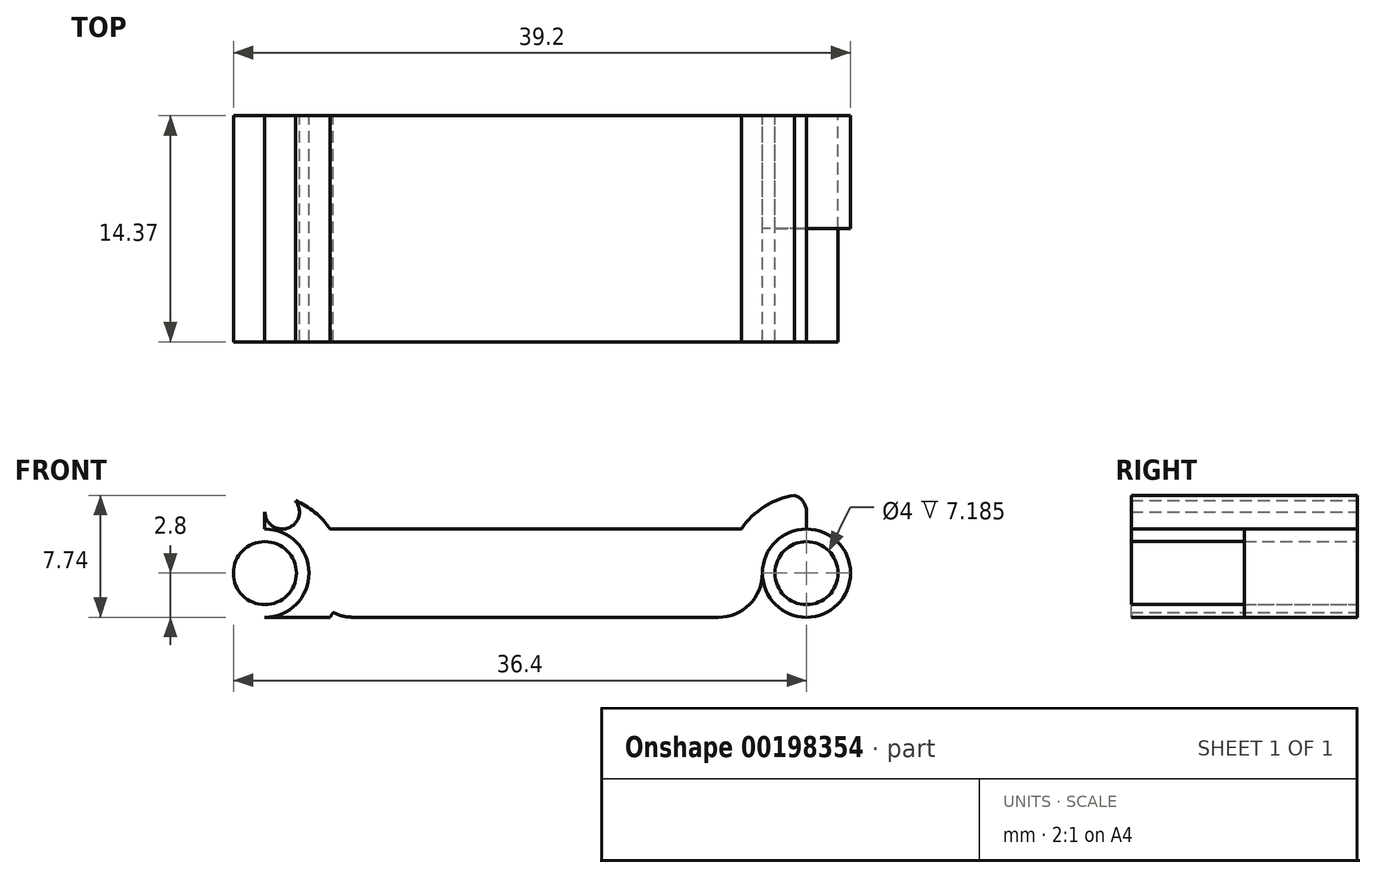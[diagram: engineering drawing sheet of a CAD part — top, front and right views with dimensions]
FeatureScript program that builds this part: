
annotation { "Feature Type Name" : "Feature", "Feature Type Description" : "" }
export const myFeature = defineFeature(function(context is Context, id is Id, definition is map)
    precondition{}
    {
        {
            var Q0;
            Q0=qCreatedBy(makeId("Front.planeOp"),FACE);
            var sketch = newSketch(context, id + "F0", { "sketchPlane" : qUnion([Q0])});
            skLineSegment(sketch, "E0.bottom", {"start": v(2.8, 0) * mm, "end": v(37.2, 0) * mm});
            skLineSegment(sketch, "E0.top", {"start": v(2.8, 5.6) * mm, "end": v(36.1, 5.6) * mm});
            skLineSegment(sketch, "E1.bottom", {"start": v(36.1, 5.6) * mm, "end": v(34.4, 5.6) * mm, "construction": true});
            skLineSegment(sketch, "E1.top", {"start": v(37.2, 0) * mm, "end": v(34.4, 0) * mm, "construction": true});
            skLineSegment(sketch, "E1.right", {"start": v(34.4, 5.6) * mm, "end": v(34.4, 0) * mm, "construction": true});
            skLineSegment(sketch, "E2", {"start": v(34.4, 5.6) * mm, "end": v(40, 0) * mm, "construction": true});
            skCircle(sketch, "E3", {"center": v(37.2, 2.8) * mm, "radius": 2 * mm});
            skCircle(sketch, "E4", {"center": v(37.2, 2.8) * mm, "radius": 2.8 * mm});
            skArc(sketch, "E5", {"start": v(36.45, 7.74) * mm, "mid": v(34.53, 7.03) * mm, "end": v(33.06, 5.6) * mm});
            skArc(sketch, "E6", {"start": v(31.6, 2.8) * mm, "mid": v(36.82, 1.4) * mm, "end": v(33, 5.22) * mm, "construction": true});
            skArc(sketch, "E7", {"start": v(31.6, 0) * mm, "mid": v(33.58, 0.82) * mm, "end": v(34.4, 2.8) * mm});
            skLineSegment(sketch, "E8", {"start": v(37.2, 2.8) * mm, "end": v(37.2, 6.7) * mm, "construction": true});
            skLineSegment(sketch, "E9", {"start": v(37.2, 6.7) * mm, "end": v(37.2, 5.6) * mm});
            skCircle(sketch, "E10", {"center": v(37.2, 6.7) * mm, "radius": 1.1 * mm, "construction": true});
            skArc(sketch, "E11", {"start": v(35.26, 7.4) * mm, "mid": v(36.4, 5.64) * mm, "end": v(36.45, 7.74) * mm});
            skLineSegment(sketch, "E12", {"start": v(20, 5.6) * mm, "end": v(20, 0) * mm, "construction": true});
            skPoint(sketch, "E13.orphan", {"position": v(40, 5.6) * mm});
            skArc(sketch, "E14.trimOffspring", {"start": v(32.74, 0.55) * mm, "mid": v(32.89, 0.27) * mm, "end": v(33.06, 0) * mm});
            skPoint(sketch, "E15.orphan", {"position": v(37.2, 7.8) * mm});
            skLineSegment(sketch, "E16.MirrorCS", {"start": v(2.8, 6.7) * mm, "end": v(2.8, 5.6) * mm});
            skArc(sketch, "E17.MirrorCS", {"start": v(7.26, 0.55) * mm, "mid": v(7.11, 0.27) * mm, "end": v(6.94, 0) * mm});
            skLineSegment(sketch, "E18.MirrorCS", {"start": v(2.8, 2.8) * mm, "end": v(2.8, 6.7) * mm, "construction": true});
            skLineSegment(sketch, "E19.MirrorCS", {"start": v(3.9, 5.6) * mm, "end": v(5.6, 5.6) * mm, "construction": true});
            skLineSegment(sketch, "E20.MirrorCS", {"start": v(2.8, 0) * mm, "end": v(5.6, 0) * mm, "construction": true});
            skArc(sketch, "E21.MirrorCS", {"start": v(4.74, 7.4) * mm, "mid": v(3.6, 5.64) * mm, "end": v(3.55, 7.74) * mm});
            skLineSegment(sketch, "E22.MirrorCS", {"start": v(5.6, 5.6) * mm, "end": v(0, 0) * mm, "construction": true});
            skLineSegment(sketch, "E23.MirrorCS", {"start": v(5.6, 5.6) * mm, "end": v(5.6, 0) * mm, "construction": true});
            skCircle(sketch, "E24.MirrorC", {"center": v(2.8, 6.7) * mm, "radius": 1.1 * mm, "construction": true});
            skArc(sketch, "E25.MirrorCS", {"start": v(8.4, 0) * mm, "mid": v(6.42, 0.82) * mm, "end": v(5.6, 2.8) * mm});
            skArc(sketch, "E26.MirrorCS", {"start": v(3.55, 7.74) * mm, "mid": v(5.47, 7.03) * mm, "end": v(6.94, 5.6) * mm});
            skPoint(sketch, "E27.MirrorP", {"position": v(0, 5.6) * mm});
            skPoint(sketch, "E28.MirrorP", {"position": v(2.8, 7.8) * mm});
            skCircle(sketch, "E29.MirrorC", {"center": v(2.8, 2.8) * mm, "radius": 2 * mm});
            skCircle(sketch, "E30.MirrorC", {"center": v(2.8, 2.8) * mm, "radius": 2.8 * mm});
            skArc(sketch, "E31.MirrorCS", {"start": v(8.4, 2.8) * mm, "mid": v(3.18, 1.4) * mm, "end": v(7, 5.22) * mm, "construction": true});
            skPoint(sketch, "E32.orphan", {"position": v(0, 0) * mm});
            skSolve(sketch);
        }
        {
            var Q0;
            {var subQ3=sQuery(id+"F0.wireOp",EDGE,"E9");Q0=makeQuery(id+"F0.imprint","IMPRINT",FACE,{"disambiguationData":[TD([[makeQuery(id+"F0.imprint","IMPRINT",EDGE,{"derivedFrom":subQ3}),-1.0]])]});}
            var Q1;
            {var subQ0=sQuery(id+"F0.wireOp",EDGE,"E11");var subQ1=sQuery(id+"F0.wireOp",EDGE,"E0.top");var subQ2=makeQuery(id+"F0.imprint","INTERSECT",VERTEX,{"derivedFrom":[subQ1,subQ0]});Q1=makeQuery(id+"F0.imprint","IMPRINT",FACE,{"disambiguationData":[TD([[makeQuery(id+"F0.imprint","IMPRINT",EDGE,{"disambiguationData":[TD([[subQ2,1.0]])],"derivedFrom":subQ1}),1.0]])]});}
            var Q2;
            {var subQ0=sQuery(id+"F0.wireOp",EDGE,"E11");var subQ1=sQuery(id+"F0.wireOp",EDGE,"E5");var subQ2=makeQuery(id+"F0.imprint","INTERSECT",VERTEX,{"disambiguationData":[OD(0.0)],"derivedFrom":[subQ1,subQ0]});Q2=makeQuery(id+"F0.imprint","IMPRINT",FACE,{"disambiguationData":[TD([[makeQuery(id+"F0.imprint","IMPRINT",EDGE,{"disambiguationData":[TD([[subQ2,-1.0]])],"derivedFrom":subQ1}),1.0]])]});}
            var Q3;
            {var subQ0=sQuery(id+"F0.wireOp",EDGE,"E26.MirrorCS");var subQ1=sQuery(id+"F0.wireOp",EDGE,"E0.top");var subQ2=makeQuery(id+"F0.imprint","INTERSECT",VERTEX,{"derivedFrom":[subQ1,subQ0]});Q3=makeQuery(id+"F0.imprint","IMPRINT",FACE,{"disambiguationData":[TD([[makeQuery(id+"F0.imprint","IMPRINT",EDGE,{"disambiguationData":[TD([[subQ2,1.0]])],"derivedFrom":subQ1}),1.0]])]});}
            var Q4;
            {var subQ0=sQuery(id+"F0.wireOp",EDGE,"E26.MirrorCS");var subQ1=sQuery(id+"F0.wireOp",EDGE,"E21.MirrorCS");var subQ2=makeQuery(id+"F0.imprint","INTERSECT",VERTEX,{"disambiguationData":[OD(0.0)],"derivedFrom":[subQ1,subQ0]});Q4=makeQuery(id+"F0.imprint","IMPRINT",FACE,{"disambiguationData":[TD([[makeQuery(id+"F0.imprint","IMPRINT",EDGE,{"disambiguationData":[TD([[subQ2,-1.0]])],"derivedFrom":subQ1}),-1.0]])]});}
            var Q5;
            Q5=makeQuery(id+"F0.imprint","IMPRINT",FACE,{"disambiguationData":[TD([[makeQuery(id+"F0.imprint","IMPRINT",EDGE,{"derivedFrom":sQuery(id+"F0.wireOp",EDGE,"E3")}),1.0]])]});
            var Q6;
            {var subQ0=sQuery(id+"F0.wireOp",EDGE,"E16.MirrorCS");Q6=makeQuery(id+"F0.imprint","IMPRINT",FACE,{"disambiguationData":[TD([[makeQuery(id+"F0.imprint","IMPRINT",EDGE,{"derivedFrom":subQ0}),1.0]])]});}
            extrude(context, id + "F1", {"entities" : qUnion([Q0, Q1, Q2, Q3, Q4, Q5, Q6]), "depth" : 14.37 * mm});
        }
        {
            var Q0;
            Q0=makeQuery(id+"F0.imprint","IMPRINT",FACE,{"disambiguationData":[TD([[makeQuery(id+"F0.imprint","IMPRINT",EDGE,{"derivedFrom":sQuery(id+"F0.wireOp",EDGE,"E3")}),-1.0]])]});
            extrude(context, id + "F2", {"entities" : qUnion([Q0]), "depth" : 7.18 * mm});
        }
        {
            var Q0;
            {var subQ0=sQuery(id+"F0.wireOp",EDGE,"E30.MirrorC");var subQ1=sQuery(id+"F0.wireOp",EDGE,"E0.bottom");var subQ2=makeQuery(id+"F0.imprint","INTERSECT",VERTEX,{"derivedFrom":[subQ1,subQ0]});Q0=makeQuery(id+"F0.imprint","IMPRINT",FACE,{"disambiguationData":[TD([[makeQuery(id+"F0.imprint","IMPRINT",EDGE,{"disambiguationData":[TD([[subQ2,-1.0]])],"derivedFrom":subQ1}),1.0]])]});}
            var Q1;
            Q1=makeQuery(id+"F0.imprint","IMPRINT",FACE,{"disambiguationData":[TD([[makeQuery(id+"F0.imprint","IMPRINT",EDGE,{"derivedFrom":sQuery(id+"F0.wireOp",EDGE,"E29.MirrorC")}),1.0]])]});
            extrude(context, id + "F3", {"entities" : qUnion([Q0, Q1]), "operationType" : NewBodyOperationType.ADD, "depth" : 14.37 * mm});
        }
    });
